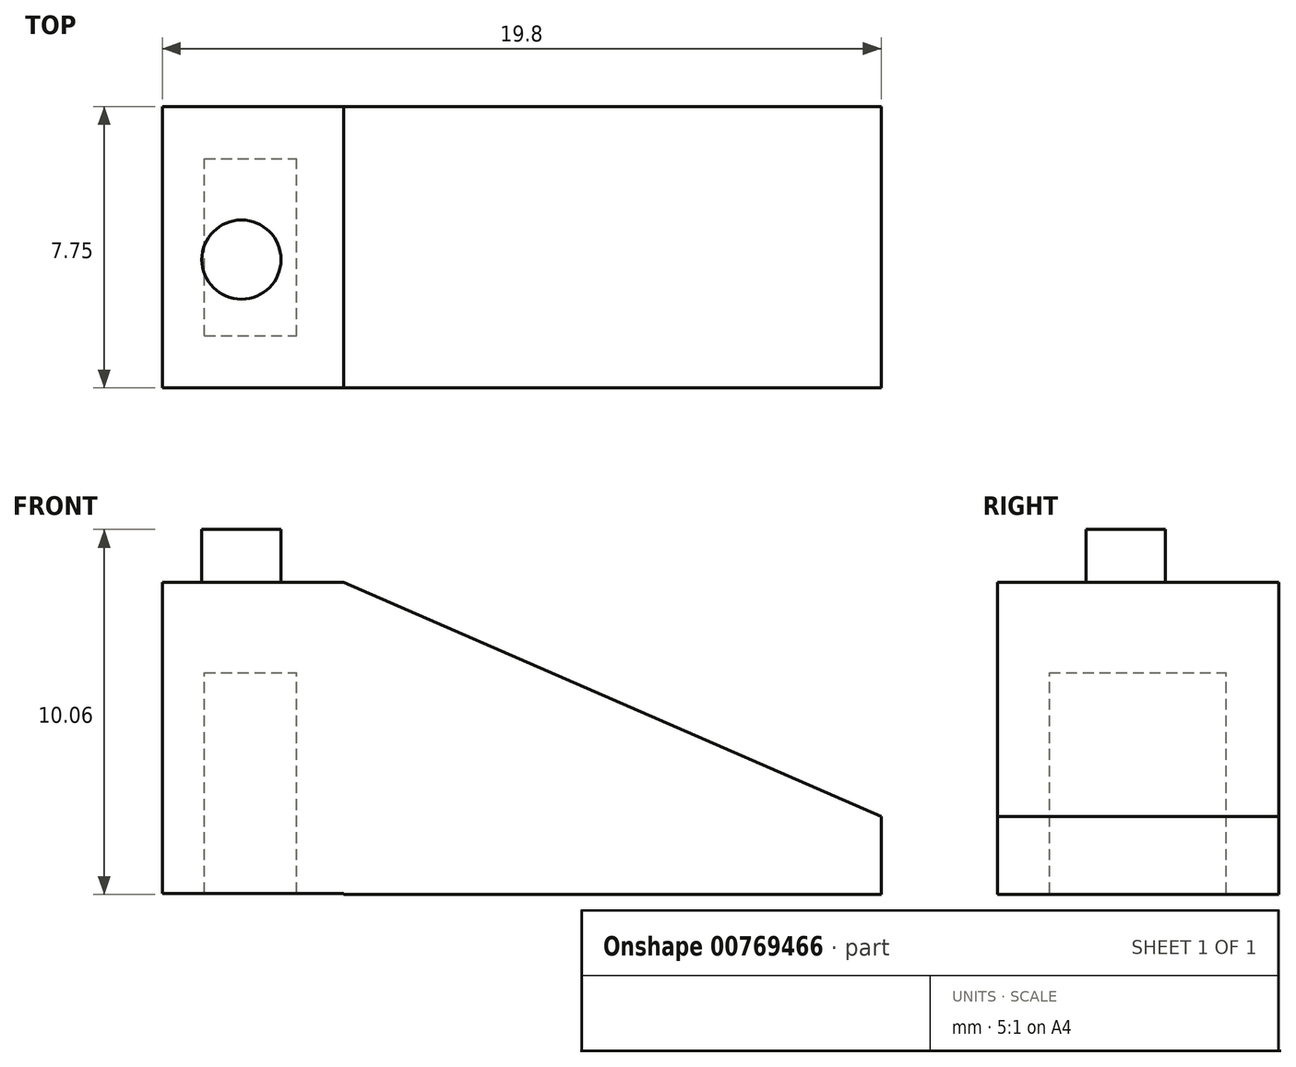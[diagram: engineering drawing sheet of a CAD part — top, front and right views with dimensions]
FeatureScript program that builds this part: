
annotation { "Feature Type Name" : "Feature", "Feature Type Description" : "" }
export const myFeature = defineFeature(function(context is Context, id is Id, definition is map)
    precondition{}
    {
        {
            var Q0;
            Q0=qCreatedBy(makeId("Front.planeOp"),FACE);
            var sketch = newSketch(context, id + "F0", { "sketchPlane" : qUnion([Q0])});
            skLineSegment(sketch, "E0.bottom", {"start": v(-1.16, 2.5) * mm, "end": v(3.84, 2.5) * mm});
            skLineSegment(sketch, "E0.top", {"start": v(-1.16, -6.08) * mm, "end": v(3.84, -6.08) * mm});
            skLineSegment(sketch, "E0.left", {"start": v(-1.16, 2.5) * mm, "end": v(-1.16, -6.08) * mm});
            skLineSegment(sketch, "E0.right", {"start": v(3.84, 2.5) * mm, "end": v(3.84, -6.08) * mm});
            skLineSegment(sketch, "E1.top", {"start": v(3.84, -6.11) * mm, "end": v(18.64, -6.11) * mm});
            skLineSegment(sketch, "E1.left", {"start": v(3.84, 2.5) * mm, "end": v(3.84, -6.11) * mm});
            skLineSegment(sketch, "E1.right", {"start": v(18.64, -3.96) * mm, "end": v(18.64, -6.11) * mm});
            skLineSegment(sketch, "E2", {"start": v(18.64, -6.11) * mm, "end": v(18.64, -3.96) * mm});
            skLineSegment(sketch, "E3", {"start": v(18.64, -3.96) * mm, "end": v(3.84, 2.5) * mm});
            skSolve(sketch);
        }
        {
            var Q0;
            Q0 = qSketchRegion(id + "F0", true);
            extrude(context, id + "F1", {"entities" : qUnion([Q0]), "depth" : 7.75 * mm, "offsetDistance" : 25 * mm});
        }
        {
            var Q0;
            Q0=qCreatedBy(makeId("Top.planeOp"),FACE);
            var sketch = newSketch(context, id + "F2", { "sketchPlane" : qUnion([Q0])});
            skLineSegment(sketch, "E4", {"start": v(-0.07, -4.22) * mm, "end": v(0, -4.22) * mm});
            skCircle(sketch, "E5", {"center": v(1.02, -4.22) * mm, "radius": 1.1 * mm});
            skPoint(sketch, "E6.end.orphan", {"position": v(2.12, -4.22) * mm});
            skPoint(sketch, "E6.start.orphan", {"position": v(3.77, -4.22) * mm});
            skPoint(sketch, "E7.orphan", {"position": v(-1.33, -4.22) * mm});
            skSolve(sketch);
        }
        {
            var Q0;
            Q0 = qSketchRegion(id + "F2", true);
            extrude(context, id + "F3", {"entities" : qUnion([Q0]), "operationType" : NewBodyOperationType.ADD, "depth" : 3.95 * mm, "offsetDistance" : 25 * mm});
        }
        {
            var Q0;
            Q0=qCreatedBy(makeId("Top.planeOp"),FACE);
            var sketch = newSketch(context, id + "F4", { "sketchPlane" : qUnion([Q0])});
            skLineSegment(sketch, "E8", {"start": v(1.4, 0) * mm, "end": v(1.4, -1.5) * mm});
            skLineSegment(sketch, "E9.bottom", {"start": v(0, -6.32) * mm, "end": v(2.54, -6.32) * mm});
            skLineSegment(sketch, "E9.top", {"start": v(0, -1.44) * mm, "end": v(2.54, -1.44) * mm});
            skLineSegment(sketch, "E9.left", {"start": v(0, -6.32) * mm, "end": v(0, -1.44) * mm});
            skLineSegment(sketch, "E9.right", {"start": v(2.54, -6.32) * mm, "end": v(2.54, -1.44) * mm});
            skPoint(sketch, "E10.end.orphan", {"position": v(0, -5.68) * mm});
            skPoint(sketch, "E10.start.orphan", {"position": v(-1.5, -5.68) * mm});
            skPoint(sketch, "E11.end.orphan", {"position": v(1.4, -6.32) * mm});
            skPoint(sketch, "E12.end.orphan", {"position": v(2.54, -4) * mm});
            skPoint(sketch, "E12.start.orphan", {"position": v(4.04, -4) * mm});
            skSolve(sketch);
        }
        {
            var Q0;
            Q0 = qSketchRegion(id + "F4", true);
            extrude(context, id + "F5", {"entities" : qUnion([Q0]), "operationType" : NewBodyOperationType.REMOVE, "oppositeDirection" : true, "depth" : 25 * mm, "offsetDistance" : 25 * mm});
        }
        {
            var Q0;
            Q0=qCreatedBy(makeId("Top.planeOp"),FACE);
            var sketch = newSketch(context, id + "F6", { "sketchPlane" : qUnion([Q0])});
            skLineSegment(sketch, "E13.top", {"start": v(3.82, 0) * mm, "end": v(2.62, 0) * mm});
            skLineSegment(sketch, "E13.left", {"start": v(3.82, -7.75) * mm, "end": v(3.82, 0) * mm});
            skLineSegment(sketch, "E13.right", {"start": v(2.62, -7.75) * mm, "end": v(2.62, 0) * mm});
            skLineSegment(sketch, "E14", {"start": v(2.62, -7.75) * mm, "end": v(3.82, -7.75) * mm});
            skSolve(sketch);
        }
        {
            var Q0;
            Q0 = qSketchRegion(id + "F6", true);
            extrude(context, id + "F7", {"entities" : qUnion([Q0]), "operationType" : NewBodyOperationType.ADD, "oppositeDirection" : true, "depth" : 6 * mm, "offsetDistance" : 25 * mm});
        }
        {
            var Q0;
            Q0 = qSketchRegion(id + "F6", true);
            extrude(context, id + "F8", {"entities" : qUnion([Q0]), "operationType" : NewBodyOperationType.ADD, "oppositeDirection" : true, "depth" : 6 * mm, "offsetDistance" : 25 * mm});
        }
    });
